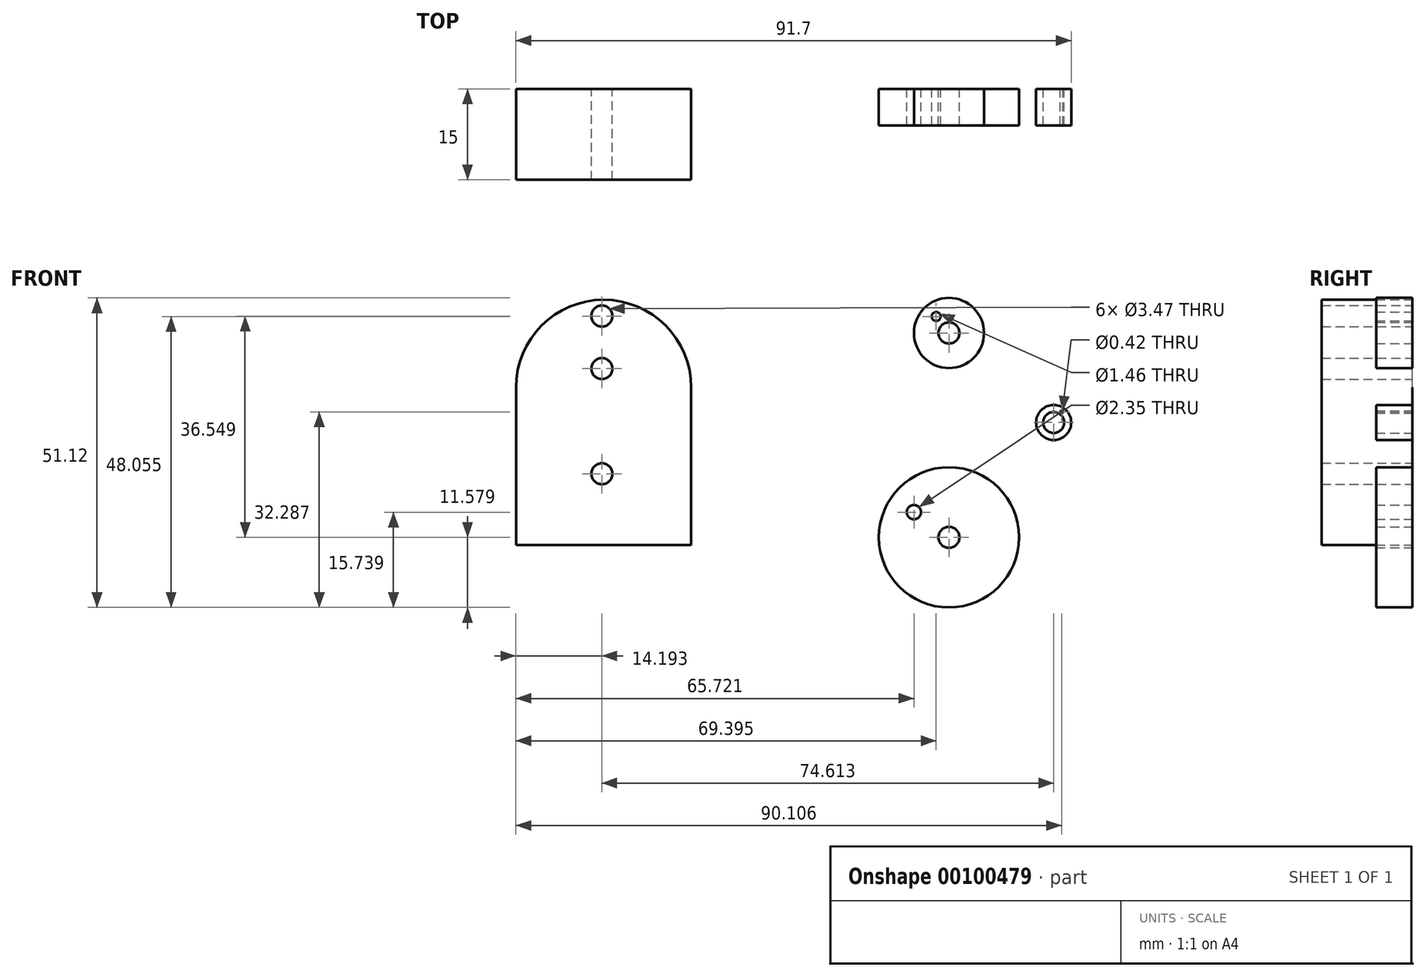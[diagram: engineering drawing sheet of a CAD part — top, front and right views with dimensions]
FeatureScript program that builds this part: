
annotation { "Feature Type Name" : "Feature", "Feature Type Description" : "" }
export const myFeature = defineFeature(function(context is Context, id is Id, definition is map)
    precondition{}
    {
        {
            var Q0;
            Q0=qCreatedBy(makeId("Front.planeOp"),FACE);
            var sketch = newSketch(context, id + "F0", { "sketchPlane" : qUnion([Q0])});
            skCircle(sketch, "E0", {"center": v(0, -18.97) * mm, "radius": 11.58 * mm});
            skCircle(sketch, "E1", {"center": v(0, 14.78) * mm, "radius": 5.79 * mm});
            skCircle(sketch, "E2", {"center": v(17.3, 0) * mm, "radius": 2.9 * mm});
            skLineSegment(sketch, "E3.bottom", {"start": v(-42.57, -20.26) * mm, "end": v(-71.5, -20.26) * mm});
            skLineSegment(sketch, "E3.top", {"start": v(-57.04, 20.26) * mm, "end": v(-57.04, 20.26) * mm});
            skLineSegment(sketch, "E3.left", {"start": v(-42.57, -20.26) * mm, "end": v(-42.57, 5.79) * mm});
            skLineSegment(sketch, "E3.right", {"start": v(-71.5, -20.26) * mm, "end": v(-71.5, 5.79) * mm});
            skPoint(sketch, "E3.middle", {"position": v(-57.04, 0) * mm});
            skPoint(sketch, "E4.visualSharp", {"position": v(-42.57, 20.26) * mm});
            skArc(sketch, "E4.filletArc", {"start": v(-42.57, 5.79) * mm, "mid": v(-46.8, 16.02) * mm, "end": v(-57.04, 20.26) * mm});
            skPoint(sketch, "E5.visualSharp", {"position": v(-71.5, 20.26) * mm});
            skArc(sketch, "E5.filletArc", {"start": v(-57.04, 20.26) * mm, "mid": v(-67.27, 16.02) * mm, "end": v(-71.5, 5.79) * mm});
            skCircle(sketch, "E6", {"center": v(0, -18.97) * mm, "radius": 1.74 * mm});
            skCircle(sketch, "E7", {"center": v(17.3, 0) * mm, "radius": 1.74 * mm});
            skCircle(sketch, "E8", {"center": v(0, 14.78) * mm, "radius": 1.74 * mm});
            skCircle(sketch, "E9", {"center": v(-57.32, -8.47) * mm, "radius": 1.74 * mm});
            skCircle(sketch, "E10", {"center": v(-57.32, 8.9) * mm, "radius": 1.74 * mm});
            skCircle(sketch, "E11", {"center": v(-57.32, 17.58) * mm, "radius": 1.74 * mm});
            skCircle(sketch, "E12", {"center": v(-5.79, -14.81) * mm, "radius": 1.17 * mm});
            skCircle(sketch, "E13", {"center": v(18.6, 1.74) * mm, "radius": 0.2 * mm});
            skCircle(sketch, "E14", {"center": v(-2.12, 17.5) * mm, "radius": 0.73 * mm});
            skSolve(sketch);
        }
        {
            var Q0;
            Q0=makeQuery(id+"F0.imprint","IMPRINT",FACE,{"disambiguationData":[TD([[makeQuery(id+"F0.imprint","IMPRINT",EDGE,{"derivedFrom":sQuery(id+"F0.wireOp",EDGE,"E3.bottom")}),-1.0]])]});
            extrude(context, id + "F1", {"entities" : qUnion([Q0]), "depth" : 15 * mm});
        }
        {
            var Q0;
            Q0=makeQuery(id+"F0.imprint","IMPRINT",FACE,{"disambiguationData":[TD([[makeQuery(id+"F0.imprint","IMPRINT",EDGE,{"derivedFrom":sQuery(id+"F0.wireOp",EDGE,"E1")}),1.0]])]});
            extrude(context, id + "F2", {"entities" : qUnion([Q0]), "depth" : 6 * mm});
        }
        {
            var Q0;
            Q0=makeQuery(id+"F0.imprint","IMPRINT",FACE,{"disambiguationData":[TD([[makeQuery(id+"F0.imprint","IMPRINT",EDGE,{"derivedFrom":sQuery(id+"F0.wireOp",EDGE,"E0")}),1.0]])]});
            extrude(context, id + "F3", {"entities" : qUnion([Q0]), "depth" : 6 * mm});
        }
        {
            var Q0;
            Q0=makeQuery(id+"F0.imprint","IMPRINT",FACE,{"disambiguationData":[TD([[makeQuery(id+"F0.imprint","IMPRINT",EDGE,{"derivedFrom":sQuery(id+"F0.wireOp",EDGE,"E2")}),1.0]])]});
            extrude(context, id + "F4", {"entities" : qUnion([Q0]), "depth" : 6 * mm});
        }
    });
